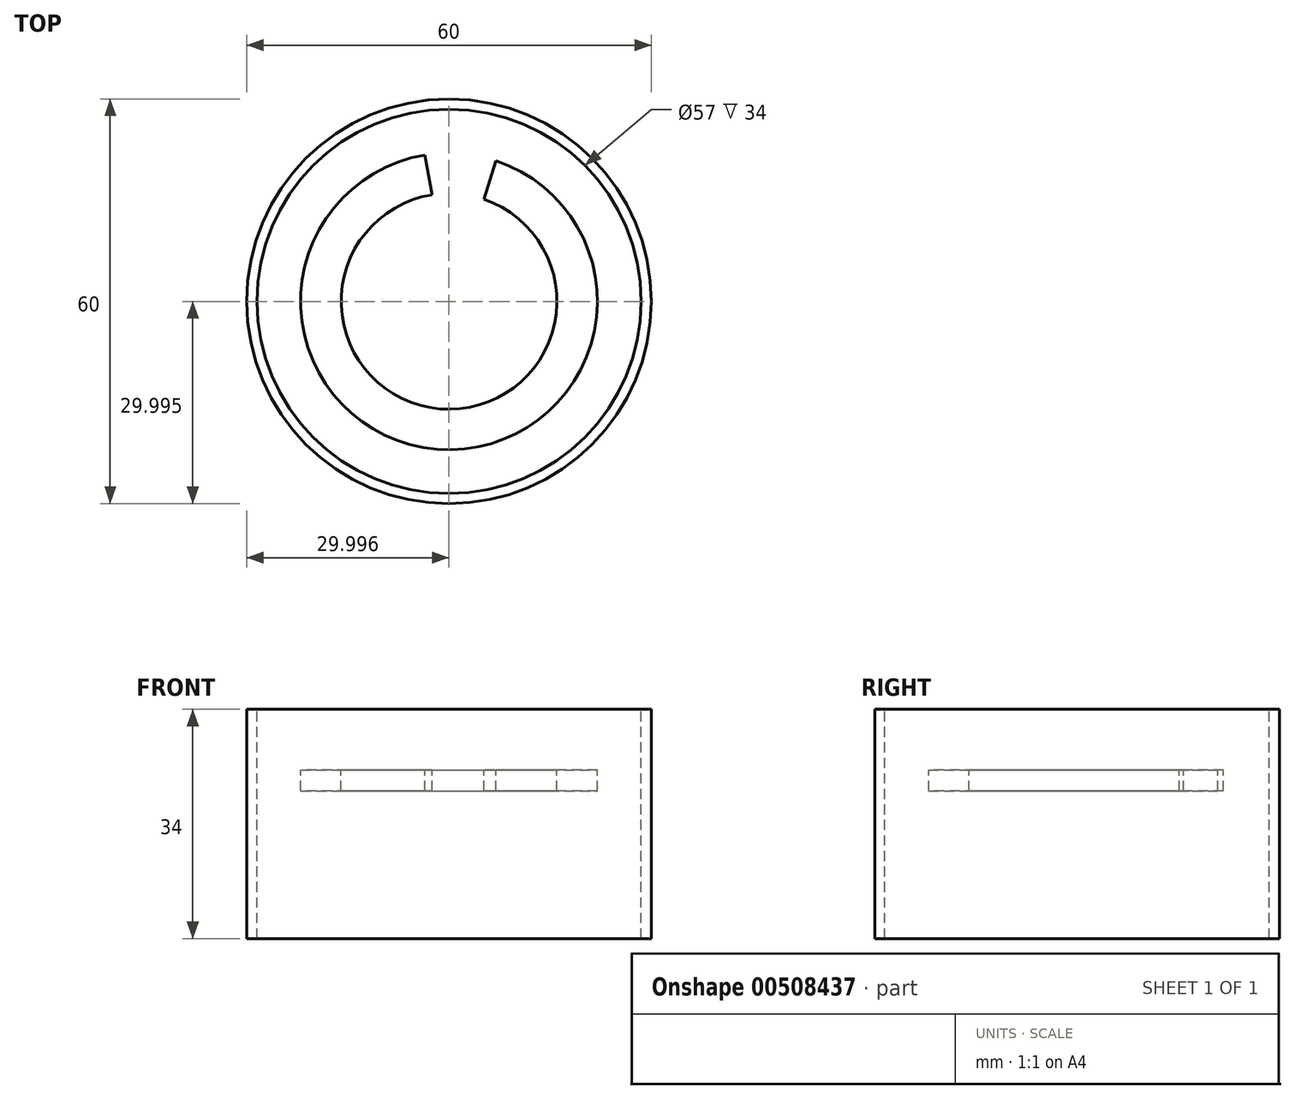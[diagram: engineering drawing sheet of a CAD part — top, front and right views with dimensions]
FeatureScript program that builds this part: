
annotation { "Feature Type Name" : "Feature", "Feature Type Description" : "" }
export const myFeature = defineFeature(function(context is Context, id is Id, definition is map)
    precondition{}
    {
        {
            var Q0;
            Q0=qCreatedBy(makeId("Top.planeOp"),FACE);
            var sketch = newSketch(context, id + "F0", { "sketchPlane" : qUnion([Q0])});
            skCircle(sketch, "E0", {"center": v(-2.7, 6.62) * mm, "radius": 28.5 * mm});
            skCircle(sketch, "E1", {"center": v(-2.7, 6.62) * mm, "radius": 30 * mm});
            skCircle(sketch, "E2", {"center": v(-2.7, 6.62) * mm, "radius": 22 * mm});
            skCircle(sketch, "E3.0", {"center": v(-2.7, 6.62) * mm, "radius": 16 * mm});
            skLineSegment(sketch, "E4", {"start": v(-6.28, 28.32) * mm, "end": v(-5.23, 22.41) * mm});
            skLineSegment(sketch, "E5", {"start": v(-5.23, 22.41) * mm, "end": v(2.47, 21.76) * mm});
            skLineSegment(sketch, "E6", {"start": v(2.47, 21.76) * mm, "end": v(4.26, 27.48) * mm});
            skLineSegment(sketch, "E7", {"start": v(4.26, 27.48) * mm, "end": v(-0.54, 30.25) * mm});
            skLineSegment(sketch, "E8", {"start": v(-0.54, 30.25) * mm, "end": v(-6.28, 28.32) * mm});
            skSolve(sketch);
        }
        {
            var Q0;
            Q0=makeQuery(id+"F0.imprint","IMPRINT",FACE,{"disambiguationData":[TD([[makeQuery(id+"F0.imprint","IMPRINT",EDGE,{"derivedFrom":sQuery(id+"F0.wireOp",EDGE,"E0")}),-1.0]])]});
            extrude(context, id + "F1", {"entities" : qUnion([Q0]), "oppositeDirection" : true, "depth" : 25 * mm});
        }
        {
            var Q0;
            {var subQ0=sQuery(id+"F0.wireOp",EDGE,"E4");Q0=makeQuery(id+"F0.imprint","IMPRINT",FACE,{"disambiguationData":[TD([[makeQuery(id+"F0.imprint","IMPRINT",EDGE,{"derivedFrom":subQ0}),-1.0]])]});}
            extrude(context, id + "F2", {"entities" : qUnion([Q0]), "oppositeDirection" : true, "depth" : 3.1 * mm, "offsetDistance" : 25 * mm});
        }
        {
            var Q0;
            Q0=makeQuery(id+"F1.opExtrude","CAP_FACE",FACE,{"disambiguationData":[OSD([sQuery(id+"F0.wireOp",EDGE,"E0"),sQuery(id+"F0.wireOp",EDGE,"E1")])],"isStart":true});
            extrude(context, id + "F3", {"entities" : qUnion([Q0]), "operationType" : NewBodyOperationType.ADD, "depth" : 9 * mm});
        }
    });
